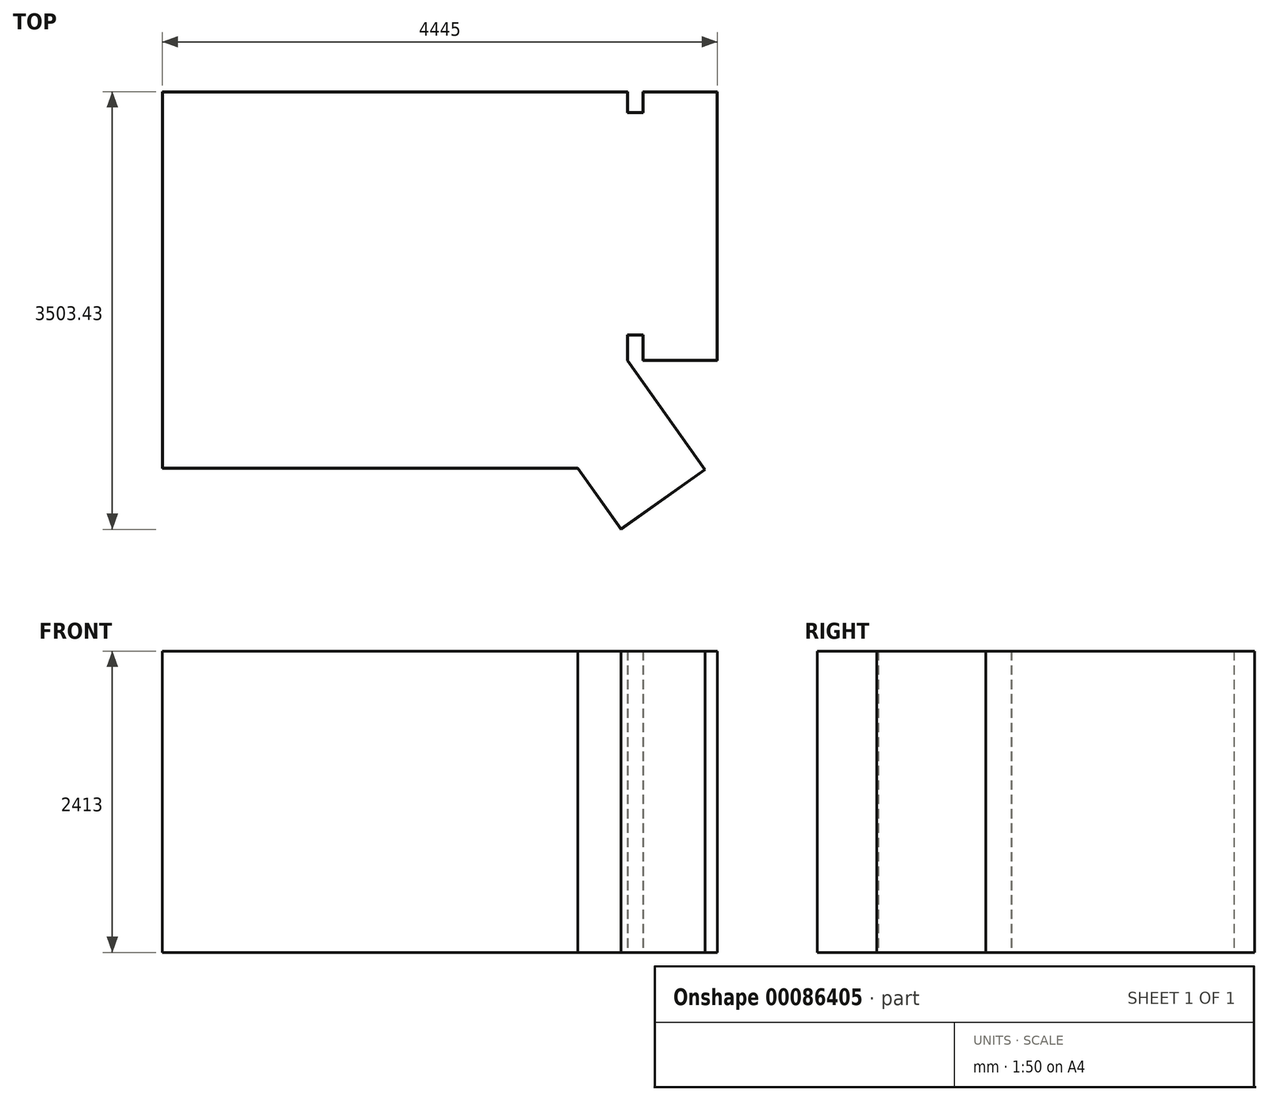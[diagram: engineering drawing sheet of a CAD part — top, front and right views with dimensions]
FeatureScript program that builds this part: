
annotation { "Feature Type Name" : "Feature", "Feature Type Description" : "" }
export const myFeature = defineFeature(function(context is Context, id is Id, definition is map)
    precondition{}
    {
        {
            var Q0;
            Q0=qCreatedBy(makeId("Top.planeOp"),FACE);
            var sketch = newSketch(context, id + "F0", { "sketchPlane" : qUnion([Q0])});
            skLineSegment(sketch, "E0", {"start": v(-3727.45, 2152.65) * mm, "end": v(0, 2152.65) * mm});
            skLineSegment(sketch, "E1", {"start": v(0, 2152.65) * mm, "end": v(0, 1987.55) * mm});
            skLineSegment(sketch, "E2", {"start": v(0, 0) * mm, "end": v(618.6, -873.8) * mm});
            skLineSegment(sketch, "E3", {"start": v(618.6, -873.8) * mm, "end": v(-55.16, -1350.78) * mm});
            skLineSegment(sketch, "E4", {"start": v(-55.16, -1350.78) * mm, "end": v(-400.05, -863.6) * mm});
            skLineSegment(sketch, "E5", {"start": v(-400.05, -863.6) * mm, "end": v(-3727.45, -863.6) * mm});
            skLineSegment(sketch, "E6", {"start": v(-3727.45, -863.6) * mm, "end": v(-3727.45, 2152.65) * mm});
            skLineSegment(sketch, "E7.bottom", {"start": v(120.65, 0) * mm, "end": v(717.55, 0) * mm});
            skLineSegment(sketch, "E7.top", {"start": v(120.65, 2152.65) * mm, "end": v(717.55, 2152.65) * mm});
            skLineSegment(sketch, "E7.left", {"start": v(120.65, 0) * mm, "end": v(120.65, 203.2) * mm});
            skLineSegment(sketch, "E7.right", {"start": v(717.55, 0) * mm, "end": v(717.55, 2152.65) * mm});
            skLineSegment(sketch, "E8", {"start": v(0, 1987.55) * mm, "end": v(120.65, 1987.55) * mm});
            skLineSegment(sketch, "E9", {"start": v(0, 203.2) * mm, "end": v(120.65, 203.2) * mm});
            skLineSegment(sketch, "E10.trimOffspring", {"start": v(0, 203.2) * mm, "end": v(0, 0) * mm});
            skLineSegment(sketch, "E11.trimOffspring", {"start": v(120.65, 1987.55) * mm, "end": v(120.65, 2152.65) * mm});
            skSolve(sketch);
        }
        {
            var Q0;
            Q0=makeQuery(id+"F0.imprint","IMPRINT",FACE,{"disambiguationData":[TD([[makeQuery(id+"F0.imprint","IMPRINT",EDGE,{"derivedFrom":sQuery(id+"F0.wireOp",EDGE,"E0")}),-1.0]])]});
            extrude(context, id + "F1", {"entities" : qUnion([Q0]), "depth" : 2413 * mm});
        }
        {
            var Q0;
            Q0=makeQuery(id+"F1.opExtrude","CAP_FACE",FACE,{"disambiguationData":[OSD([sQuery(id+"F0.wireOp",EDGE,"E0"),sQuery(id+"F0.wireOp",EDGE,"E1"),sQuery(id+"F0.wireOp",EDGE,"E2"),sQuery(id+"F0.wireOp",EDGE,"E3"),sQuery(id+"F0.wireOp",EDGE,"E4"),sQuery(id+"F0.wireOp",EDGE,"E5"),sQuery(id+"F0.wireOp",EDGE,"E6"),sQuery(id+"F0.wireOp",EDGE,"E7.bottom"),sQuery(id+"F0.wireOp",EDGE,"E7.top"),sQuery(id+"F0.wireOp",EDGE,"E7.left"),sQuery(id+"F0.wireOp",EDGE,"E7.right"),sQuery(id+"F0.wireOp",EDGE,"E8"),sQuery(id+"F0.wireOp",EDGE,"E9"),sQuery(id+"F0.wireOp",EDGE,"E10.trimOffspring"),sQuery(id+"F0.wireOp",EDGE,"E11.trimOffspring")])],"isStart":false});
            shell(context, id + "F2", {"entities" : qUnion([Q0]), "thickness" : 2.54 * mm});
        }
    });
